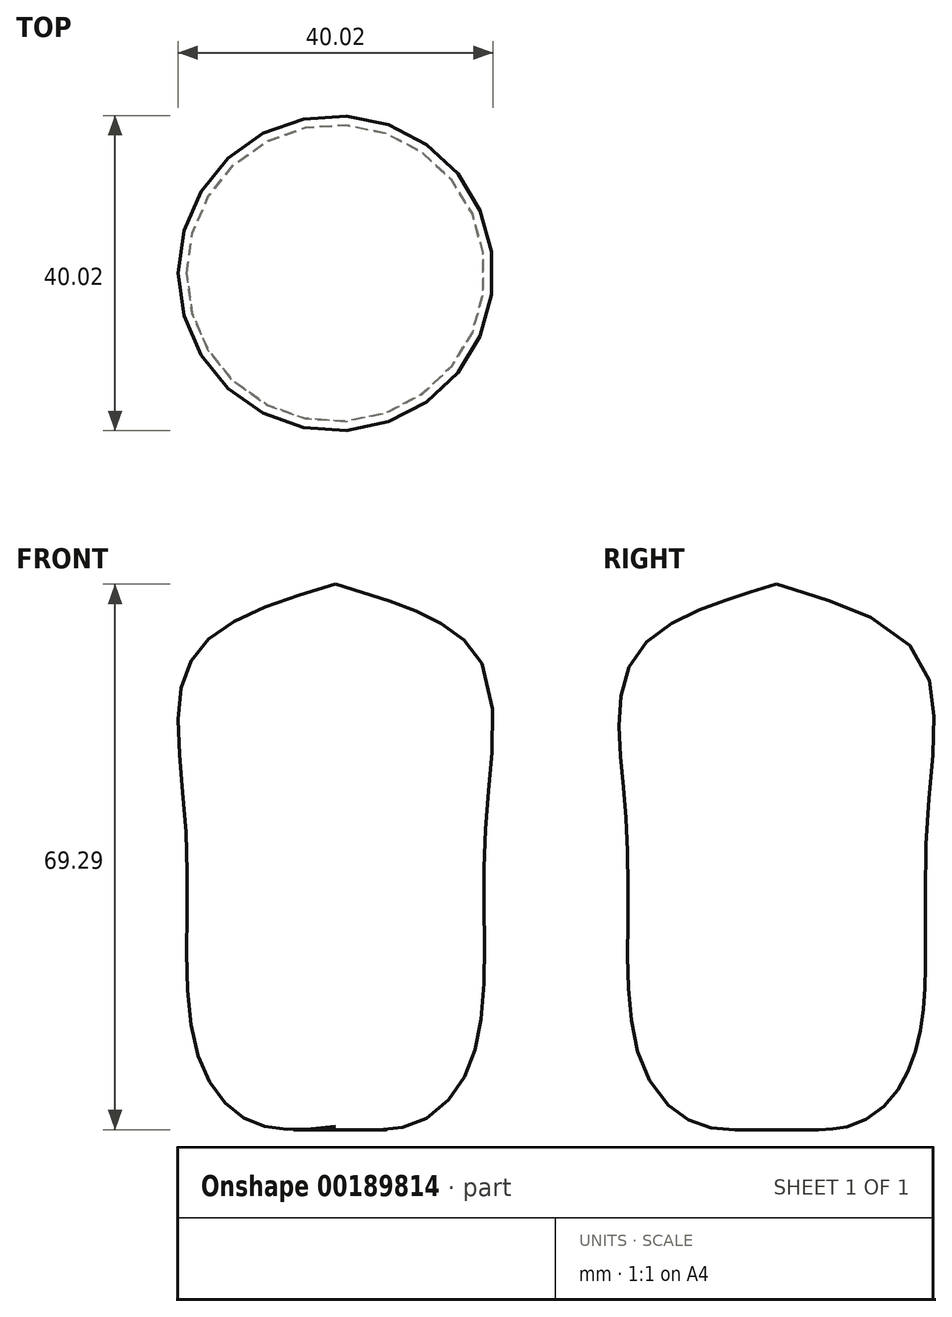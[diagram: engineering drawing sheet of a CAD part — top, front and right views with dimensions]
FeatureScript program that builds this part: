
annotation { "Feature Type Name" : "Feature", "Feature Type Description" : "" }
export const myFeature = defineFeature(function(context is Context, id is Id, definition is map)
    precondition{}
    {
        {
            var Q0;
            Q0=qCreatedBy(makeId("Front.planeOp"),FACE);
            var sketch = newSketch(context, id + "F0", { "sketchPlane" : qUnion([Q0])});
            skFitSpline(sketch, "E0", {"points": [v(0, -37.13) * mm, v(-10.45, -36.64) * mm, v(-17.78, -27.11) * mm, v(-19, 0) * mm, v(-18.27, 22.23) * mm, v(0, 31.76) * mm], "startDerivative": vector(-72.03, -8.02) * mm, "endDerivative": vector(106.86, 31.41) * mm});
            skLineSegment(sketch, "E1", {"start": v(0, 31.76) * mm, "end": v(0, -37.13) * mm});
            skSolve(sketch);
        }
        {
            var Q0;
            Q0 = qSketchRegion(id + "F0", true);
            var Q1;
            Q1=sQuery(id+"F0.wireOp",EDGE,"E1");
            revolve(context, id + "F1", {"entities" : qUnion([Q0]), "axis" : qUnion([Q1]), "revolveType" : RevolveType.FULL});
        }
    });
